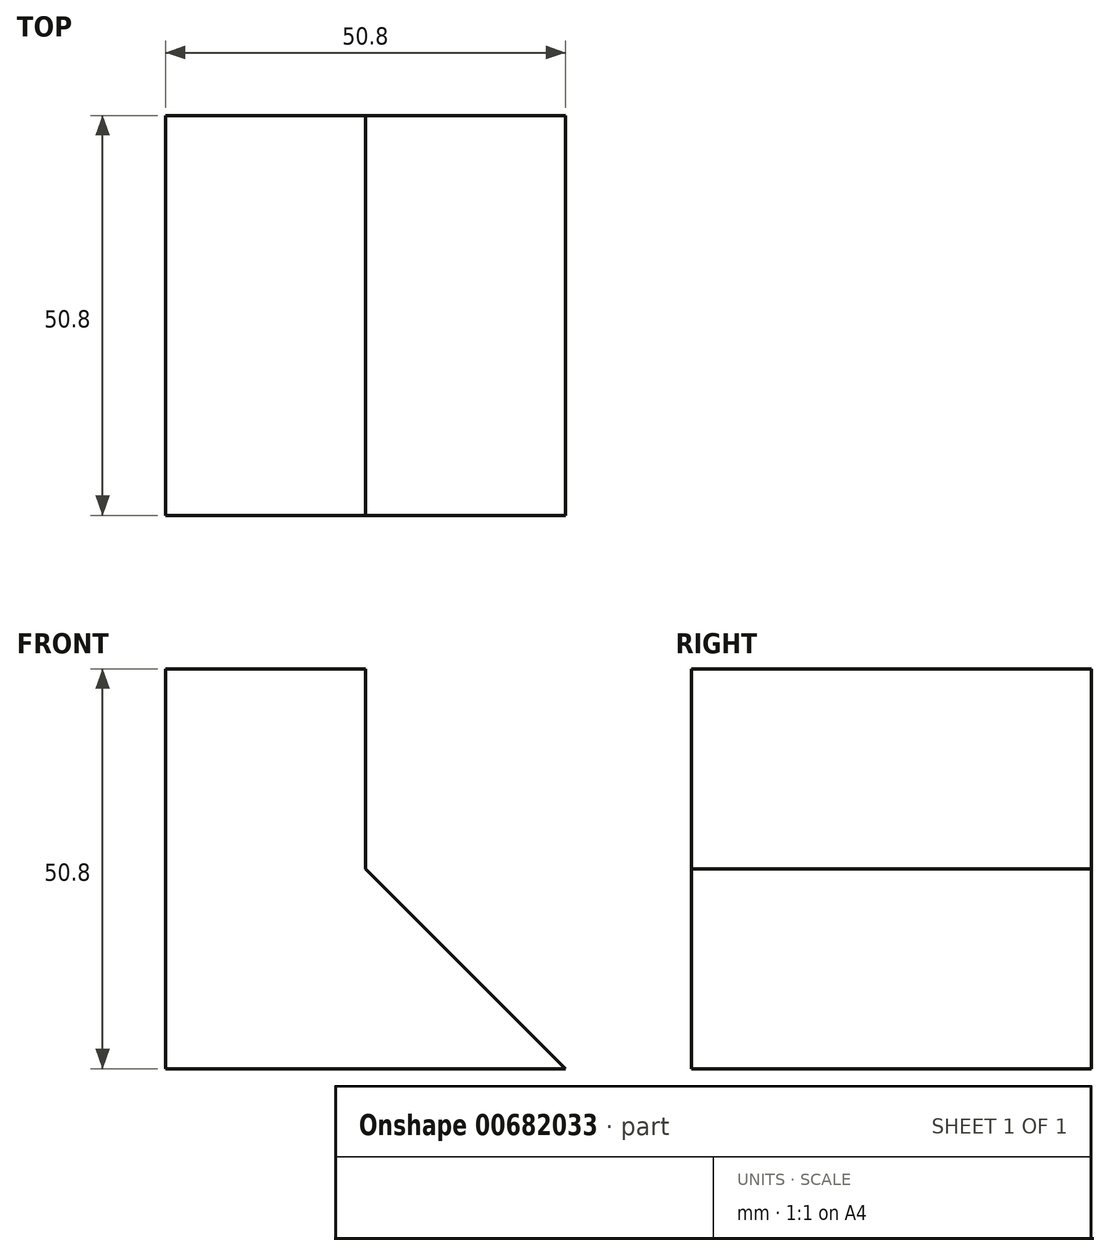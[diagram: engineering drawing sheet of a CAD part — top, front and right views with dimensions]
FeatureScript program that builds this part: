
annotation { "Feature Type Name" : "Feature", "Feature Type Description" : "" }
export const myFeature = defineFeature(function(context is Context, id is Id, definition is map)
    precondition{}
    {
        {
            var Q0;
            Q0=qCreatedBy(makeId("Front.planeOp"),FACE);
            var sketch = newSketch(context, id + "F0", { "sketchPlane" : qUnion([Q0])});
            skLineSegment(sketch, "E0", {"start": v(-46.69, 50.8) * mm, "end": v(-46.69, 0) * mm});
            skLineSegment(sketch, "E1", {"start": v(-46.69, 0) * mm, "end": v(4.11, 0) * mm});
            skLineSegment(sketch, "E2", {"start": v(-46.69, 50.8) * mm, "end": v(-21.29, 50.8) * mm});
            skLineSegment(sketch, "E3", {"start": v(-21.29, 50.8) * mm, "end": v(-21.29, 25.4) * mm});
            skLineSegment(sketch, "E4", {"start": v(-21.29, 25.4) * mm, "end": v(4.11, 0) * mm});
            skSolve(sketch);
        }
        {
            var Q0;
            Q0 = qSketchRegion(id + "F0", true);
            extrude(context, id + "F1", {"entities" : qUnion([Q0]), "depth" : 50.8 * mm, "offsetDistance" : 25.4 * mm});
        }
    });
